# Revit family: 54-3132-001 DN1100
name_source: partatom
category: Pipe Accessories
units: mm (PartAtom-declared; Revit-internal decimal feet)

## family parameters
Always vertical = No
Cut with Voids When Loaded = No
Part Type = Valve - Breaks Into
Round Connector Dimension = Use Diameter
Shared = No
Work Plane-Based = No

## types (9) — shared parameters
1 = 1 mm  [stored 0.00328084 ft]
10 = 10 mm  [stored 0.0328084 ft]
54-1100-31-0302100 = DN1100_ PN10_ CTC
54-1100-31-0303100 = DN1100_ PN10_ CTC
54-1100-31-0304100 = DN1100_ PN10_ CTC
54-1100-31-1302100 = DN1100_ PN16_ CTC
54-1100-31-1303100 = DN1100_ PN16_ CTC
54-1100-32-0302100 = DN1100_ PN10_ CTO
54-1100-32-0303100 = DN1100_ PN10_ CTO
54-1100-32-1302100 = DN1100_ PN16_ CTO
54-1100-32-1303100 = DN1100_ PN16_ CTO
ACtuator_T = 38.52 mm  [stored 0.126378 ft]
ADN = 1100 mm
Actuator_FLR = 105 mm  [stored 0.344488 ft]
Actuator_angle = 103.92 mm
Actuator_dim1 = 63 mm  [stored 0.206693 ft]
Actuator_dim2 = 37.8 mm  [stored 0.124016 ft]
BP_centre = 35 mm  [stored 0.114829 ft]
Body_H = 1191 mm
Body_L = 1204 mm
Body_T = 542.5 mm  [stored 1.77986 ft]
Body_W = 504.75 mm
Body_rib_T = 21.4 mm  [stored 0.07021 ft]
Bonnet_FL_L = 1505 mm
Bonnet_FL_T = 101.65 mm  [stored 0.333497 ft]
Bonnet_FL_W = 673 mm
Bonnet_dim1 = 240.8 mm  [stored 0.790026 ft]
Bonnet_dim2 = 176.66 mm
Bonnet_dim3 = 2048.52 mm
Bonnet_fillet = 56.08 mm
Bore = 550.08 mm  [stored 1.80472 ft]
Bypass_Arc = 65 mm  [stored 0.213255 ft]
Bypass_Location = 180 mm  [stored 0.590551 ft]
Bypass_R = 70 mm  [stored 0.229659 ft]
Bypass_R1 = 140 mm  [stored 0.459318 ft]
Bypass_T = 26 mm
Bypass_W = 82 mm  [stored 0.269029 ft]
Bypass_dis = 60 mm  [stored 0.19685 ft]
Bypass_shaft = 140 mm  [stored 0.459318 ft]
Cut_dis = 50.83 mm
DN = 1100.16 mm
Description_ = AVK METAL SEAT GATE VALVE, FLANGED, PN 10/16
F = 42 mm  [stored 0.137795 ft]
F1 = 18.9 mm  [stored 0.0620079 ft]
F2 = 160 mm  [stored 0.524934 ft]
FL_T = 53.5 mm  [stored 0.175525 ft]
Fillet = 168.25 mm  [stored 0.552001 ft]
H1 = 2382 mm
H2 = 700 mm
L = 811 mm
OD = 1400 mm
OD1 = 1400 mm
PN = 16 mm  [stored 0.0524934 ft]
Raised_dia = 1218 mm
Raised_dis = 5 mm  [stored 0.0164042 ft]
Rib_Actual = 752.5 mm
Rib_H = 952.8 mm
Rib_H1 = 260 mm  [stored 0.853018 ft]
Rib_H2 = 715 mm
Rib_H3 = 815 mm
Rib_H4 = 915 mm
Rib_L = 677.25 mm
Rib_W = 302.85 mm  [stored 0.993602 ft]
Search_table = 54-3132-001 DN1100
Stem_dim = 52.5 mm  [stored 0.172244 ft]
URL product pages = https://www.avkvalves.com
W = 1505 mm
W1 = 627 mm  [stored 2.05709 ft]
W_half = 878 mm
bottom_rib = 700 mm
stem_dim = 53.33 mm
stem_dim1 = 68.25 mm  [stored 0.223917 ft]
sweep = 6 mm  [stored 0.019685 ft]
wedge_dim1 = 555.23 mm
zero-valued in all types: Default Elevation

## per-type parameters (varying)
| type | H |
| 54-1100-31-0302100 | 1100 mm |
| 54-1100-31-0303100 | 1100.11 mm |
| 54-1100-31-0304100 | 1100.13 mm |
| 54-1100-31-1302100 | 1100.14 mm |
| 54-1100-31-1303100 | 1100.15 mm |
| 54-1100-32-0302100 | 1100.16 mm |
| 54-1100-32-0303100 | 1100.17 mm |
| 54-1100-32-1302100 | 1100.18 mm |
| 54-1100-32-1303100 | 1100.19 mm |

note: [stored X ft] marks values corroborated as IEEE doubles in the binary element streams (Revit-internal decimal feet)

## geometry (parser evidence)
native form markers: Sweep x4
no freeform markers — native parametric forms only
